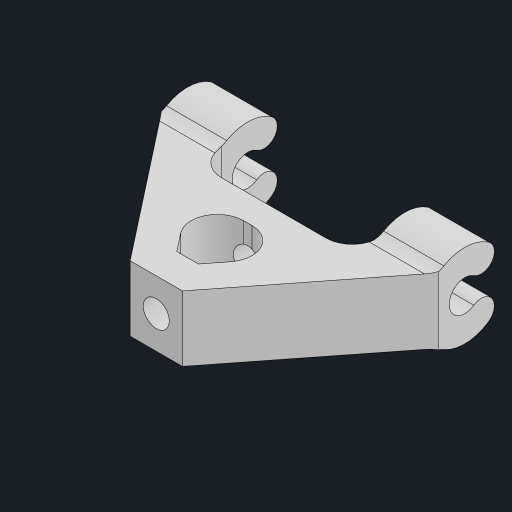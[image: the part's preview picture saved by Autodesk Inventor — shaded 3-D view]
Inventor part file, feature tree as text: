
AUTODESK INVENTOR PART (.ipt)
format: ipt  version: 2023 (Build 270158000, 158)  size: 198,144 bytes
history: native  units: mm
features: sketch x3, extrude x3, other x1, hole x1, mirror x1, fillet x1
ambient origin geometry x8: Origin, YZ Plane, XZ Plane, XY Plane, X Axis, Y Axis, Z Axis, Center Point
bodies: Body1 (feature_tree)
feature tree (10):
  other  "ソリッド1"
  sketch  "スケッチ1"
  extrude  "押し出し1"  Depth=4.0mm
  hole  "穴1"  [1 undecoded]
  sketch  "スケッチ4"
  extrude  "押し出し3"  Depth=13.0mm
  extrude  "押し出し4"  Depth=2.4mm
  mirror  "ミラー1"
  fillet  "フィレット2"  Radius=5.0mm
  sketch  "スケッチ3"
note: 1 required parameter value undecoded (feature->parameter linkage not recoverable at this tier; creation-order binding heuristic only, values carry confidence <= 0.55)
